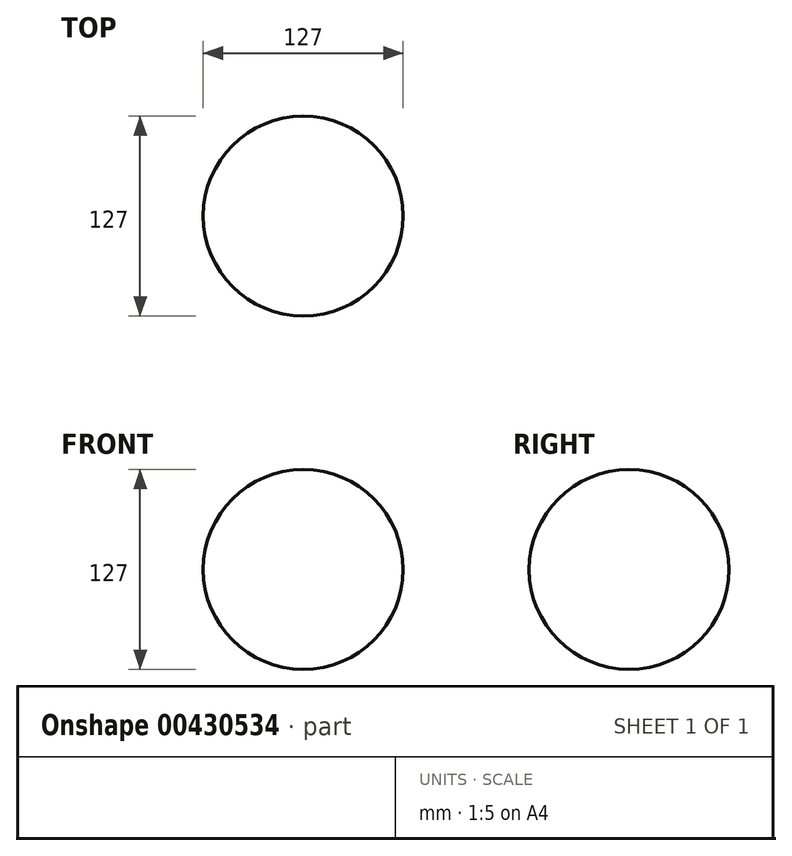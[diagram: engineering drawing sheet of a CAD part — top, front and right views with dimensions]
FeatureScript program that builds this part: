
annotation { "Feature Type Name" : "Feature", "Feature Type Description" : "" }
export const myFeature = defineFeature(function(context is Context, id is Id, definition is map)
    precondition{}
    {
        {
            var Q0;
            Q0=qCreatedBy(makeId("Front.planeOp"),FACE);
            var sketch = newSketch(context, id + "F0", { "sketchPlane" : qUnion([Q0])});
            skLineSegment(sketch, "E0", {"start": v(0, 0) * mm, "end": v(0, 127) * mm});
            skArc(sketch, "E1", {"start": v(0, 0) * mm, "mid": v(63.5, 63.5) * mm, "end": v(0, 127) * mm});
            skSolve(sketch);
        }
        {
            var Q0;
            Q0=makeQuery(id+"F0.imprint","IMPRINT",FACE,{"disambiguationData":[TD([[makeQuery(id+"F0.imprint","IMPRINT",EDGE,{"derivedFrom":sQuery(id+"F0.wireOp",EDGE,"E0")}),-1.0]])]});
            var Q1;
            Q1=sQuery(id+"F0.wireOp",EDGE,"E0");
            revolve(context, id + "F1", {"entities" : qUnion([Q0]), "axis" : qUnion([Q1]), "revolveType" : RevolveType.FULL});
        }
    });
